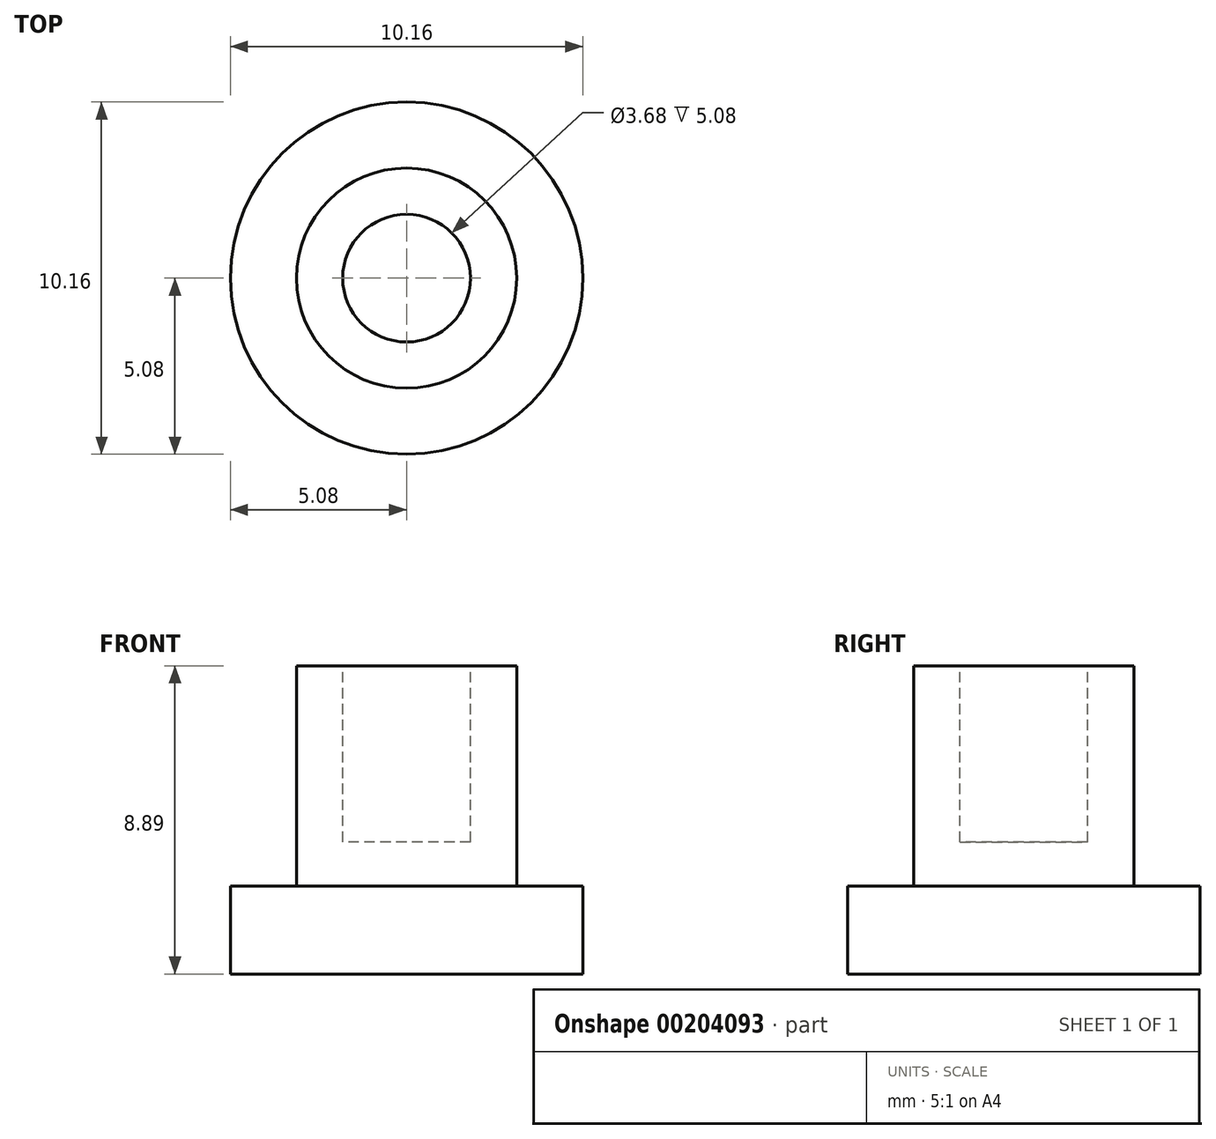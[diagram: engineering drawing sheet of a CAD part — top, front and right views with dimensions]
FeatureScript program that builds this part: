
annotation { "Feature Type Name" : "Feature", "Feature Type Description" : "" }
export const myFeature = defineFeature(function(context is Context, id is Id, definition is map)
    precondition{}
    {
        {
            var Q0;
            Q0=qCreatedBy(makeId("Top.planeOp"),FACE);
            var sketch = newSketch(context, id + "F0", { "sketchPlane" : qUnion([Q0])});
            skCircle(sketch, "E0", {"center": v(0, 0) * mm, "radius": 3.18 * mm});
            skCircle(sketch, "E1", {"center": v(0, 0) * mm, "radius": 5.08 * mm});
            skSolve(sketch);
        }
        {
            var Q0;
            Q0=makeQuery(id+"F0.imprint","IMPRINT",FACE,{"disambiguationData":[TD([[makeQuery(id+"F0.imprint","IMPRINT",EDGE,{"derivedFrom":sQuery(id+"F0.wireOp",EDGE,"E0")}),1.0]])]});
            extrude(context, id + "F1", {"entities" : qUnion([Q0]), "depth" : 8.9 * mm});
        }
        {
            var Q0;
            Q0=makeQuery(id+"F1.opExtrude","CAP_FACE",FACE,{"disambiguationData":[OSD([sQuery(id+"F0.wireOp",EDGE,"E0")])],"isStart":false});
            var sketch = newSketch(context, id + "F2", { "sketchPlane" : qUnion([Q0])});
            skCircle(sketch, "E2", {"center": v(0, 0) * mm, "radius": 1.84 * mm});
            skSolve(sketch);
        }
        {
            var Q0;
            Q0=makeQuery(id+"F2.imprint","IMPRINT",FACE,{"disambiguationData":[TD([[makeQuery(id+"F2.imprint","IMPRINT",EDGE,{"derivedFrom":sQuery(id+"F2.wireOp",EDGE,"E2")}),1.0]])]});
            extrude(context, id + "F3", {"entities" : qUnion([Q0]), "operationType" : NewBodyOperationType.REMOVE, "oppositeDirection" : true, "depth" : 5.08 * mm});
        }
        {
            var Q0;
            Q0=makeQuery(id+"F0.imprint","IMPRINT",FACE,{"disambiguationData":[TD([[makeQuery(id+"F0.imprint","IMPRINT",EDGE,{"derivedFrom":sQuery(id+"F0.wireOp",EDGE,"E0")}),-1.0]])]});
            extrude(context, id + "F4", {"entities" : qUnion([Q0]), "operationType" : NewBodyOperationType.ADD, "depth" : 2.54 * mm});
        }
    });
